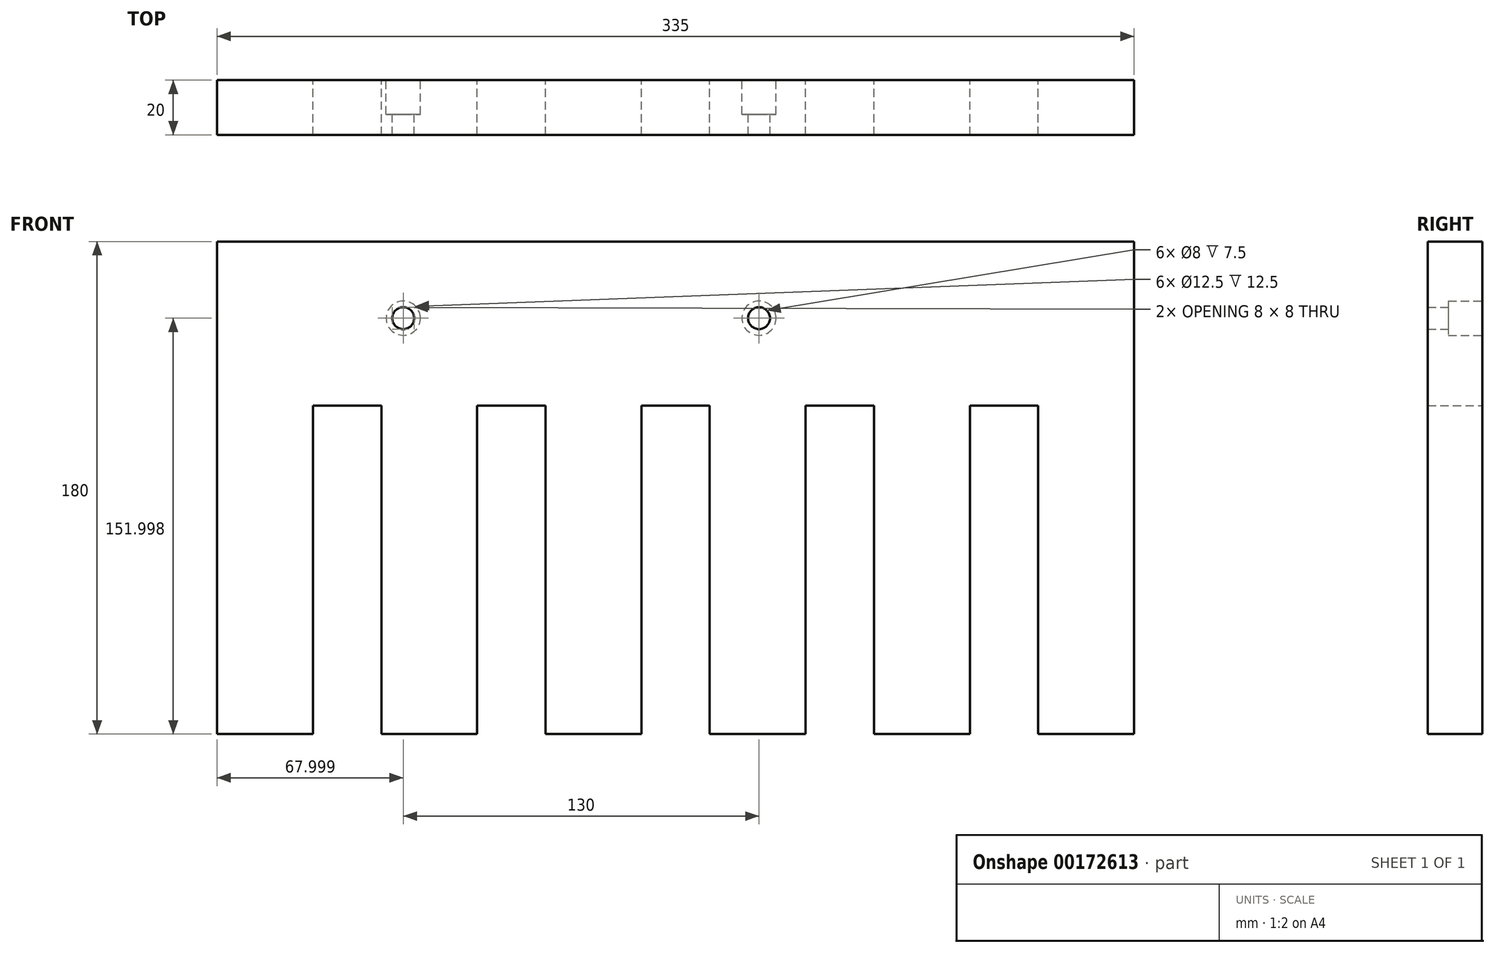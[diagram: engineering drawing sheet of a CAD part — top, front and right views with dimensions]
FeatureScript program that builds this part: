
annotation { "Feature Type Name" : "Feature", "Feature Type Description" : "" }
export const myFeature = defineFeature(function(context is Context, id is Id, definition is map)
    precondition{}
    {
        {
            var Q0;
            Q0=qCreatedBy(makeId("Front.planeOp"),FACE);
            var sketch = newSketch(context, id + "F0", { "sketchPlane" : qUnion([Q0])});
            skLineSegment(sketch, "E0", {"start": v(-137.92, 58.53) * mm, "end": v(197.08, 58.53) * mm});
            skLineSegment(sketch, "E1", {"start": v(197.08, 58.53) * mm, "end": v(197.08, -121.47) * mm});
            skLineSegment(sketch, "E2", {"start": v(197.08, -121.47) * mm, "end": v(162.08, -121.47) * mm});
            skLineSegment(sketch, "E3", {"start": v(162.08, -121.47) * mm, "end": v(162.08, -1.47) * mm});
            skLineSegment(sketch, "E4", {"start": v(162.08, -1.47) * mm, "end": v(137.08, -1.47) * mm});
            skLineSegment(sketch, "E5", {"start": v(137.08, -1.47) * mm, "end": v(137.08, -121.47) * mm});
            skLineSegment(sketch, "E6", {"start": v(137.08, -121.47) * mm, "end": v(102.08, -121.47) * mm});
            skLineSegment(sketch, "E7", {"start": v(102.08, -121.47) * mm, "end": v(102.08, -1.47) * mm});
            skLineSegment(sketch, "E8", {"start": v(102.08, -1.47) * mm, "end": v(77.08, -1.47) * mm});
            skLineSegment(sketch, "E9", {"start": v(77.08, -1.47) * mm, "end": v(77.08, -121.47) * mm});
            skPoint(sketch, "E9.endSnap0", {"position": v(119.58, -121.47) * mm});
            skLineSegment(sketch, "E10", {"start": v(77.08, -121.47) * mm, "end": v(42.08, -121.47) * mm});
            skLineSegment(sketch, "E11", {"start": v(42.08, -121.47) * mm, "end": v(42.08, -1.47) * mm});
            skLineSegment(sketch, "E12", {"start": v(42.08, -1.47) * mm, "end": v(17.08, -1.47) * mm});
            skLineSegment(sketch, "E13", {"start": v(17.08, -1.47) * mm, "end": v(17.08, -121.47) * mm});
            skLineSegment(sketch, "E14", {"start": v(17.08, -121.47) * mm, "end": v(-17.92, -121.47) * mm});
            skLineSegment(sketch, "E15", {"start": v(-17.92, -121.47) * mm, "end": v(-17.92, -1.47) * mm});
            skLineSegment(sketch, "E16", {"start": v(-17.92, -1.47) * mm, "end": v(-42.92, -1.47) * mm});
            skLineSegment(sketch, "E17", {"start": v(-42.92, -1.47) * mm, "end": v(-42.92, -121.47) * mm});
            skLineSegment(sketch, "E18", {"start": v(-42.92, -121.47) * mm, "end": v(-77.92, -121.47) * mm});
            skLineSegment(sketch, "E19", {"start": v(-77.92, -121.47) * mm, "end": v(-77.92, -1.47) * mm});
            skLineSegment(sketch, "E20", {"start": v(-77.92, -1.47) * mm, "end": v(-102.92, -1.47) * mm});
            skLineSegment(sketch, "E21", {"start": v(-102.92, -1.47) * mm, "end": v(-102.92, -121.47) * mm});
            skLineSegment(sketch, "E22", {"start": v(-102.92, -121.47) * mm, "end": v(-137.92, -121.47) * mm});
            skLineSegment(sketch, "E23", {"start": v(-137.92, -121.47) * mm, "end": v(-137.92, 58.53) * mm});
            skPoint(sketch, "E24", {"position": v(-69.92, 30.53) * mm});
            skPoint(sketch, "E25.MirrorP", {"position": v(60.08, 30.53) * mm});
            skSolve(sketch);
        }
        {
            var Q0;
            Q0=makeQuery(id+"F0.imprint","IMPRINT",FACE,{"disambiguationData":[TD([[makeQuery(id+"F0.imprint","IMPRINT",EDGE,{"derivedFrom":sQuery(id+"F0.wireOp",EDGE,"E0")}),-1.0]])]});
            extrude(context, id + "F1", {"entities" : qUnion([Q0]), "depth" : 20 * mm});
        }
        {
            var Q0;
            Q0=sQuery(id+"F0.wireOp",VERTEX,"E24");
            var Q1;
            Q1=makeQuery(id+"F1.opExtrude","SWEPT_BODY",BODY,{"disambiguationData":[OSD([sQuery(id+"F0.wireOp",EDGE,"E0"),sQuery(id+"F0.wireOp",EDGE,"E1"),sQuery(id+"F0.wireOp",EDGE,"E2"),sQuery(id+"F0.wireOp",EDGE,"E3"),sQuery(id+"F0.wireOp",EDGE,"E4"),sQuery(id+"F0.wireOp",EDGE,"E5"),sQuery(id+"F0.wireOp",EDGE,"E6"),sQuery(id+"F0.wireOp",EDGE,"E7"),sQuery(id+"F0.wireOp",EDGE,"E8"),sQuery(id+"F0.wireOp",EDGE,"E9"),sQuery(id+"F0.wireOp",EDGE,"E10"),sQuery(id+"F0.wireOp",EDGE,"E11"),sQuery(id+"F0.wireOp",EDGE,"E12"),sQuery(id+"F0.wireOp",EDGE,"E13"),sQuery(id+"F0.wireOp",EDGE,"E14"),sQuery(id+"F0.wireOp",EDGE,"E15"),sQuery(id+"F0.wireOp",EDGE,"E16"),sQuery(id+"F0.wireOp",EDGE,"E17"),sQuery(id+"F0.wireOp",EDGE,"E18"),sQuery(id+"F0.wireOp",EDGE,"E19"),sQuery(id+"F0.wireOp",EDGE,"E20"),sQuery(id+"F0.wireOp",EDGE,"E21"),sQuery(id+"F0.wireOp",EDGE,"E22"),sQuery(id+"F0.wireOp",EDGE,"E23")])]});
            hole(context, id + "F2", {"style" : HoleStyle.C_BORE, "endStyle" : HoleEndStyle.THROUGH, "oppositeDirection" : true, "holeDiameter" : 8 * mm, "cBoreDiameter" : 12.5 * mm, "cBoreDepth" : 12.5 * mm, "locations" : qUnion([Q0]), "scope" : qUnion([Q1]), "isTappedThrough" : true});
        }
        {
            var Q0;
            Q0=sQuery(id+"F0.wireOp",VERTEX,"E25.MirrorP");
            var Q1;
            Q1=makeQuery(id+"F1.opExtrude","SWEPT_BODY",BODY,{"disambiguationData":[OSD([sQuery(id+"F0.wireOp",EDGE,"E0"),sQuery(id+"F0.wireOp",EDGE,"E1"),sQuery(id+"F0.wireOp",EDGE,"E2"),sQuery(id+"F0.wireOp",EDGE,"E3"),sQuery(id+"F0.wireOp",EDGE,"E4"),sQuery(id+"F0.wireOp",EDGE,"E5"),sQuery(id+"F0.wireOp",EDGE,"E6"),sQuery(id+"F0.wireOp",EDGE,"E7"),sQuery(id+"F0.wireOp",EDGE,"E8"),sQuery(id+"F0.wireOp",EDGE,"E9"),sQuery(id+"F0.wireOp",EDGE,"E10"),sQuery(id+"F0.wireOp",EDGE,"E11"),sQuery(id+"F0.wireOp",EDGE,"E12"),sQuery(id+"F0.wireOp",EDGE,"E13"),sQuery(id+"F0.wireOp",EDGE,"E14"),sQuery(id+"F0.wireOp",EDGE,"E15"),sQuery(id+"F0.wireOp",EDGE,"E16"),sQuery(id+"F0.wireOp",EDGE,"E17"),sQuery(id+"F0.wireOp",EDGE,"E18"),sQuery(id+"F0.wireOp",EDGE,"E19"),sQuery(id+"F0.wireOp",EDGE,"E20"),sQuery(id+"F0.wireOp",EDGE,"E21"),sQuery(id+"F0.wireOp",EDGE,"E22"),sQuery(id+"F0.wireOp",EDGE,"E23")])]});
            hole(context, id + "F3", {"style" : HoleStyle.C_BORE, "endStyle" : HoleEndStyle.THROUGH, "oppositeDirection" : true, "holeDiameter" : 8 * mm, "cBoreDiameter" : 12.5 * mm, "cBoreDepth" : 12.5 * mm, "locations" : qUnion([Q0]), "scope" : qUnion([Q1]), "isTappedThrough" : true});
        }
    });
